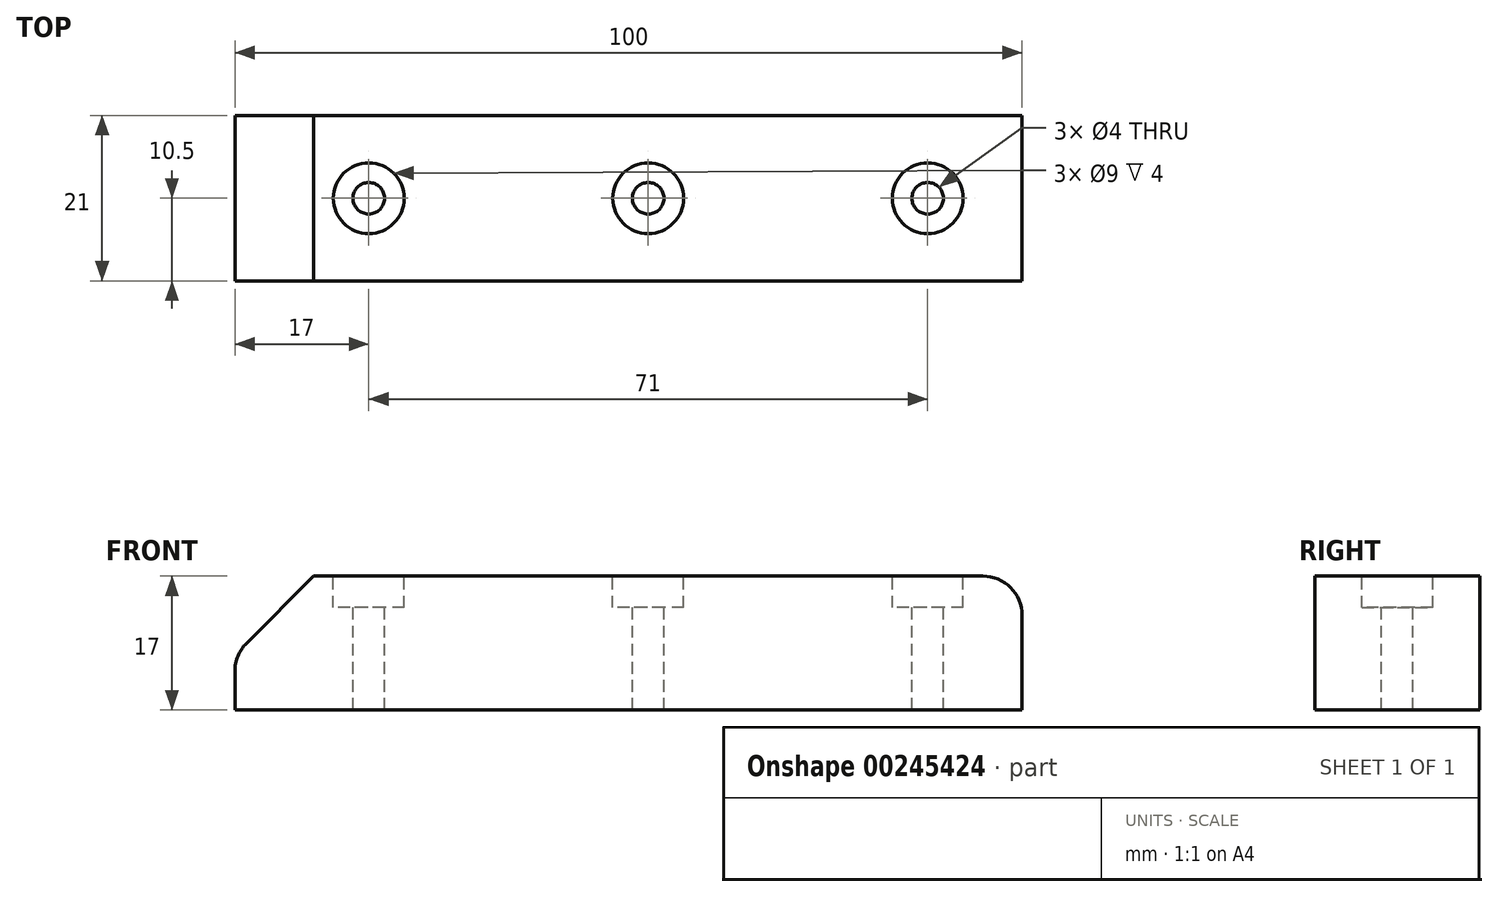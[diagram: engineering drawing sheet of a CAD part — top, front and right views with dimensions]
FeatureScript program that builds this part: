
annotation { "Feature Type Name" : "Feature", "Feature Type Description" : "" }
export const myFeature = defineFeature(function(context is Context, id is Id, definition is map)
    precondition{}
    {
        {
            var Q0;
            Q0=qCreatedBy(makeId("Front.planeOp"),FACE);
            var sketch = newSketch(context, id + "F0", { "sketchPlane" : qUnion([Q0])});
            skLineSegment(sketch, "E0.bottom", {"start": v(-3, 0) * mm, "end": v(97, 0) * mm});
            skLineSegment(sketch, "E0.top", {"start": v(7, 17) * mm, "end": v(97, 17) * mm});
            skLineSegment(sketch, "E0.right", {"start": v(97, 0) * mm, "end": v(97, 17) * mm});
            skLineSegment(sketch, "E1", {"start": v(-3, 0) * mm, "end": v(-3, 7) * mm});
            skLineSegment(sketch, "E2", {"start": v(-3, 7) * mm, "end": v(7, 17) * mm});
            skLineSegment(sketch, "E3", {"start": v(-3, 7) * mm, "end": v(9.09, 7) * mm});
            skSolve(sketch);
        }
        {
            var Q0;
            Q0=qSketchRegion(id+"F0",true);
            extrude(context, id + "F1", {"entities" : qUnion([Q0]), "depth" : 21 * mm});
        }
        {
            var Q0;
            Q0=makeQuery(id+"F1.opExtrude","SWEPT_EDGE",EDGE,{"disambiguationData":[OSD([sQuery(id+"F0.wireOp",EDGE,"E0.top"),sQuery(id+"F0.wireOp",EDGE,"E0.right")])]});
            fillet(context, id + "F2", {"entities" : qUnion([Q0]), "radius" : 5 * mm, "tangentPropagation" : true, "allowEdgeOverflow" : false});
        }
        {
            var Q0;
            Q0=makeQuery(id+"F1.opExtrude","SWEPT_EDGE",EDGE,{"disambiguationData":[OSD([sQuery(id+"F0.wireOp",EDGE,"E1"),sQuery(id+"F0.wireOp",EDGE,"E2")])]});
            fillet(context, id + "F3", {"entities" : qUnion([Q0]), "radius" : 5 * mm, "tangentPropagation" : true, "allowEdgeOverflow" : false});
        }
        {
            var Q0;
            Q0=makeQuery(id+"F1.opExtrude","SWEPT_FACE",FACE,{"disambiguationData":[OSD([sQuery(id+"F0.wireOp",EDGE,"E0.top")])]});
            var sketch = newSketch(context, id + "F4", { "sketchPlane" : qUnion([Q0])});
            skLineSegment(sketch, "E4", {"start": v(7, -10.5) * mm, "end": v(21, -10.5) * mm});
            skCircle(sketch, "E5", {"center": v(14, -10.5) * mm, "radius": 2 * mm});
            skLineSegment(sketch, "E6", {"start": v(92, -10.5) * mm, "end": v(78, -10.5) * mm});
            skCircle(sketch, "E7", {"center": v(85, -10.5) * mm, "radius": 2 * mm});
            skLineSegment(sketch, "E8", {"start": v(21, -10.5) * mm, "end": v(78, -10.5) * mm});
            skCircle(sketch, "E9", {"center": v(49.5, -10.5) * mm, "radius": 2 * mm});
            skSolve(sketch);
        }
        {
            var Q0;
            Q0=qSketchRegion(id+"F4",true);
            extrude(context, id + "F5", {"entities" : qUnion([Q0]), "operationType" : NewBodyOperationType.REMOVE, "oppositeDirection" : true, "depth" : 25 * mm});
        }
        {
            var Q0;
            Q0=makeQuery(id+"F1.opExtrude","SWEPT_FACE",FACE,{"disambiguationData":[OSD([sQuery(id+"F0.wireOp",EDGE,"E0.top")])]});
            var sketch = newSketch(context, id + "F6", { "sketchPlane" : qUnion([Q0])});
            skCircle(sketch, "E10", {"center": v(14, -10.5) * mm, "radius": 4.5 * mm});
            skCircle(sketch, "E11", {"center": v(49.5, -10.5) * mm, "radius": 4.5 * mm});
            skCircle(sketch, "E12", {"center": v(85, -10.5) * mm, "radius": 4.5 * mm});
            skSolve(sketch);
        }
        {
            var Q0;
            Q0=qSketchRegion(id+"F6",true);
            extrude(context, id + "F7", {"entities" : qUnion([Q0]), "operationType" : NewBodyOperationType.REMOVE, "oppositeDirection" : true, "depth" : 4 * mm});
        }
    });
